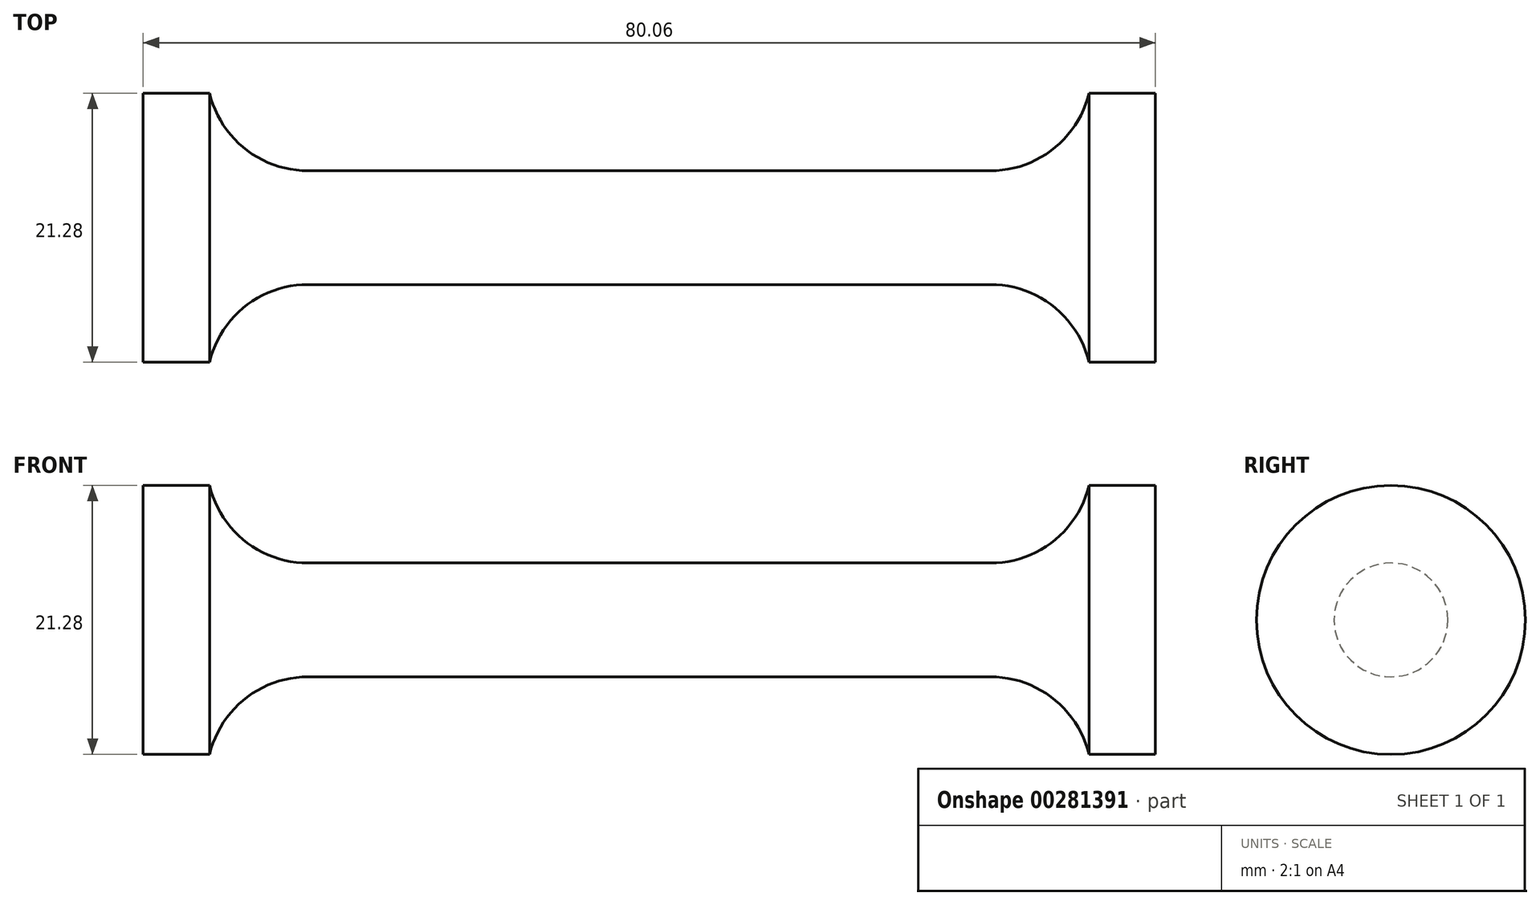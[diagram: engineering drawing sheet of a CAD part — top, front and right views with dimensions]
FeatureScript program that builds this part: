
annotation { "Feature Type Name" : "Feature", "Feature Type Description" : "" }
export const myFeature = defineFeature(function(context is Context, id is Id, definition is map)
    precondition{}
    {
        {
            var Q0;
            Q0=qCreatedBy(makeId("Front.planeOp"),FACE);
            var sketch = newSketch(context, id + "F0", { "sketchPlane" : qUnion([Q0])});
            skLineSegment(sketch, "E0", {"start": v(0, 4.5) * mm, "end": v(27, 4.5) * mm});
            skArc(sketch, "E1", {"start": v(27, 4.5) * mm, "mid": v(31.96, 6.22) * mm, "end": v(34.78, 10.64) * mm});
            skLineSegment(sketch, "E2", {"start": v(34.78, 10.64) * mm, "end": v(40.03, 10.64) * mm});
            skLineSegment(sketch, "E3", {"start": v(40.03, 10.64) * mm, "end": v(40.03, 0) * mm});
            skLineSegment(sketch, "E4.MirrorCS", {"start": v(0, 4.5) * mm, "end": v(-27, 4.5) * mm});
            skLineSegment(sketch, "E5.MirrorCS", {"start": v(-40.03, 10.64) * mm, "end": v(-40.03, 0) * mm});
            skLineSegment(sketch, "E6.MirrorCS", {"start": v(-34.78, 10.64) * mm, "end": v(-40.03, 10.64) * mm});
            skArc(sketch, "E7.MirrorCS", {"start": v(-27, 4.5) * mm, "mid": v(-31.96, 6.22) * mm, "end": v(-34.78, 10.64) * mm});
            skLineSegment(sketch, "E8", {"start": v(-40.03, 0) * mm, "end": v(40.03, 0) * mm});
            skSolve(sketch);
        }
        {
            var Q0;
            Q0=makeQuery(id+"F0.imprint","IMPRINT",FACE,{"disambiguationData":[TD([[makeQuery(id+"F0.imprint","IMPRINT",EDGE,{"derivedFrom":sQuery(id+"F0.wireOp",EDGE,"E0")}),-1.0]])]});
            var Q1;
            Q1=sQuery(id+"F0.wireOp",EDGE,"E8");
            revolve(context, id + "F1", {"entities" : qUnion([Q0]), "axis" : qUnion([Q1]), "revolveType" : RevolveType.FULL});
        }
    });
